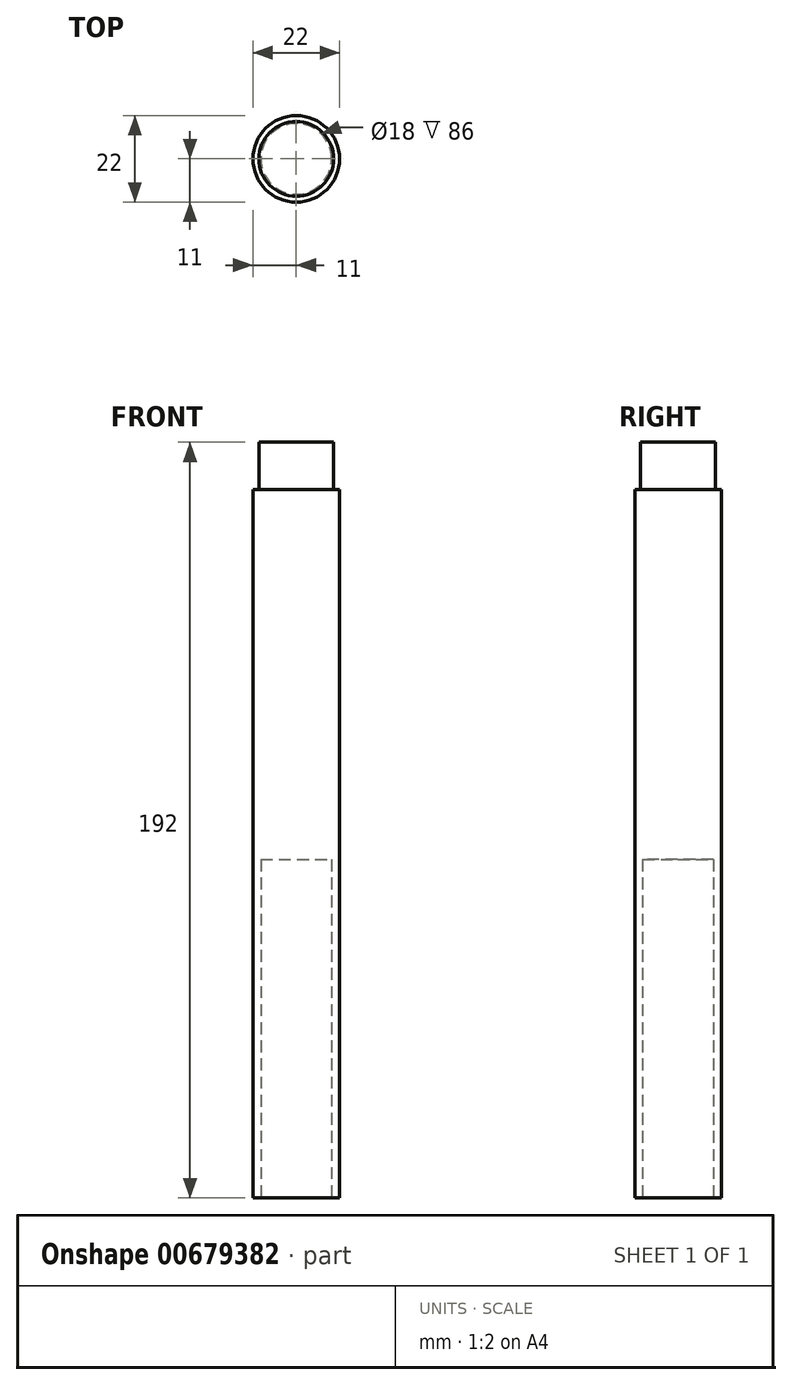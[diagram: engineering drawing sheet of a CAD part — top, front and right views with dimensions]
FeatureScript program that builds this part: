
annotation { "Feature Type Name" : "Feature", "Feature Type Description" : "" }
export const myFeature = defineFeature(function(context is Context, id is Id, definition is map)
    precondition{}
    {
        {
            var Q0;
            Q0=qCreatedBy(makeId("Top.planeOp"),FACE);
            var sketch = newSketch(context, id + "F0", { "sketchPlane" : qUnion([Q0])});
            skCircle(sketch, "E0", {"center": v(0, 0) * mm, "radius": 11 * mm});
            skSolve(sketch);
        }
        {
            var Q0;
            Q0=makeQuery(id+"F0.imprint","IMPRINT",FACE,{"disambiguationData":[TD([[makeQuery(id+"F0.imprint","IMPRINT",EDGE,{"derivedFrom":sQuery(id+"F0.wireOp",EDGE,"E0")}),1.0]])]});
            extrude(context, id + "F1", {"entities" : qUnion([Q0]), "depth" : 180 * mm, "offsetDistance" : 25 * mm});
        }
        {
            var Q0;
            Q0=makeQuery(id+"F1.opExtrude","CAP_FACE",FACE,{"disambiguationData":[OSD([sQuery(id+"F0.wireOp",EDGE,"E0")])],"isStart":false});
            var sketch = newSketch(context, id + "F2", { "sketchPlane" : qUnion([Q0])});
            skCircle(sketch, "E1", {"center": v(0, 0) * mm, "radius": 9.5 * mm});
            skSolve(sketch);
        }
        {
            var Q0;
            Q0=makeQuery(id+"F2.imprint","IMPRINT",FACE,{"disambiguationData":[TD([[makeQuery(id+"F2.imprint","IMPRINT",EDGE,{"derivedFrom":sQuery(id+"F2.wireOp",EDGE,"E1")}),1.0]])]});
            extrude(context, id + "F3", {"entities" : qUnion([Q0]), "operationType" : NewBodyOperationType.ADD, "depth" : 12 * mm, "offsetDistance" : 25 * mm});
        }
        {
            var Q0;
            Q0=makeQuery(id+"F1.opExtrude","CAP_FACE",FACE,{"disambiguationData":[OSD([sQuery(id+"F0.wireOp",EDGE,"E0")])],"isStart":true});
            var sketch = newSketch(context, id + "F4", { "sketchPlane" : qUnion([Q0])});
            skCircle(sketch, "E2", {"center": v(0, 0) * mm, "radius": 9 * mm});
            skSolve(sketch);
        }
        {
            var Q0;
            Q0=makeQuery(id+"F4.imprint","IMPRINT",FACE,{"disambiguationData":[TD([[makeQuery(id+"F4.imprint","IMPRINT",EDGE,{"derivedFrom":sQuery(id+"F4.wireOp",EDGE,"E2")}),1.0]])]});
            extrude(context, id + "F5", {"entities" : qUnion([Q0]), "operationType" : NewBodyOperationType.REMOVE, "oppositeDirection" : true, "depth" : 86 * mm, "offsetDistance" : 25 * mm});
        }
    });
